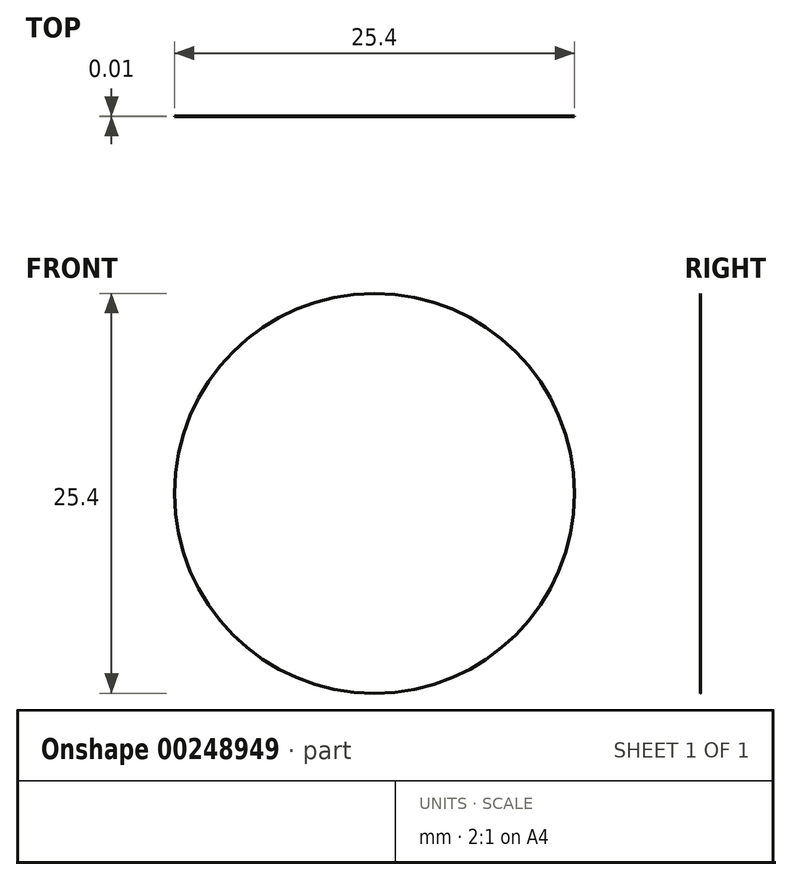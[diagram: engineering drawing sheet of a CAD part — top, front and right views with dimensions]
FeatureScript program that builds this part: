
annotation { "Feature Type Name" : "Feature", "Feature Type Description" : "" }
export const myFeature = defineFeature(function(context is Context, id is Id, definition is map)
    precondition{}
    {
        {
            var Q0;
            Q0=qCreatedBy(makeId("Front.planeOp"),FACE);
            var sketch = newSketch(context, id + "F0", { "sketchPlane" : qUnion([Q0])});
            skCircle(sketch, "E0", {"center": v(0, 0) * mm, "radius": 12.7 * mm});
            skSolve(sketch);
        }
        {
            var Q0;
            Q0=makeQuery(id+"F0.imprint","IMPRINT",FACE,{"disambiguationData":[TD([[makeQuery(id+"F0.imprint","IMPRINT",EDGE,{"derivedFrom":sQuery(id+"F0.wireOp",EDGE,"E0")}),1.0]])]});
            extrude(context, id + "F1", {"entities" : qUnion([Q0]), "depth" : 3 / 203.2 * mm});
        }
    });
